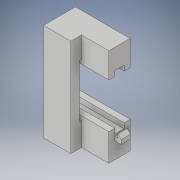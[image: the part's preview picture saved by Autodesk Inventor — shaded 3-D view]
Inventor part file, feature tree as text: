
AUTODESK INVENTOR PART (.ipt)
format: ipt  version: 2018 (Build 220112000, 112)  size: 337,920 bytes
history: native  units: in
note: dims shown in document units (in); Inventor stores cm internally (conversion verified against a paired STEP export)
features: extrude x19, sketch x18, projected_geometry x9, mirror x2, plane x1
ambient origin geometry x8: Origin, YZ Plane, XZ Plane, XY Plane, X Axis, Y Axis, Z Axis, Center Point
bodies: Solid1 (feature_tree)
feature tree (49):
  extrude  "Extrusion1"  Depth=9.0in
  extrude  "Extrusion2"  Depth=15.7in
  extrude  "Extrusion3"  Depth=0.5in
  extrude  "Extrusion4"  Depth=0.5in TaperAngle=0.0deg
  extrude  "Extrusion5"  Depth=1.05in
  extrude  "Extrusion6"  Depth=18.0in TaperAngle=0.0deg
  extrude  "Extrusion7"  Depth=3.25in
  extrude  "Extrusion11"  Depth=3.45in
  extrude  "Extrusion12"  Depth=3.25in
  plane  "Work Plane1"
  mirror  "Mirror1"
  extrude  "Extrusion14"  Depth=2.1in TaperAngle=0.0deg
  extrude  "Extrusion15"  Depth=0.75in TaperAngle=0.0deg
  extrude  "Extrusion16"  Depth=0.75in
  extrude  "Extrusion17"  Depth=0.75in
  mirror  "Mirror2"
  extrude  "Extrusion18"  Depth=4.95in
  extrude  "Extrusion19"  Depth=4.95in
  extrude  "Extrusion20"  TaperAngle=0.0deg  [1 undecoded]
  extrude  "Extrusion8"  Depth=1.5in TaperAngle=0.0deg
  extrude  "Extrusion9"  Depth=0.12in
  extrude  "Extrusion10"  Depth=0.14in
  sketch  "Sketch1"  dims[d0=16.7in d1=9.0in]
  sketch  "Sketch2"  dims[d2=6.5in d3=0.0in d4=15.7in]
  sketch  "Sketch4"  dims[d5=6.5in d6=0.5in]
  projected_geometry  "Projected Loop1"
  sketch  "Sketch5"  dims[d7=0.5in d8=5.85in d9=0.0in]
  projected_geometry  "Projected Loop2"
  sketch  "Sketch7"  dims[d10=3.775in d11=1.05in]
  projected_geometry  "Projected Loop4"
  sketch  "Sketch8"  dims[d12=2.475in d13=18.0in d14=0.0in]
  projected_geometry  "Projected Loop5"
  sketch  "Sketch9"  dims[d15=3.45in d16=3.25in]
  projected_geometry  "Projected Loop6"
  sketch  "Sketch10"  dims[d17=2.3in d18=3.45in]
  projected_geometry  "Projected Loop7"
  sketch  "Sketch11"  dims[d19=3.7in d20=3.25in]
  sketch  "Sketch12"  dims[d21=3.0in d22=0.0in d23=2.1in d24=0.0in]
  projected_geometry  "Projected Loop8"
  sketch  "Sketch13"  dims[d25=0.75in d26=0.0in d27=0.75in d28=0.0in]
  projected_geometry  "Projected Loop9"
  sketch  "Sketch15"  dims[d29=0.75in d30=0.75in]
  sketch  "Sketch17"  dims[d31=0.75in d32=0.75in]
  sketch  "Sketch18"  dims[d33=4.95in d34=4.95in]
  sketch  "Sketch19"  dims[d35=4.95in d36=4.95in]
  projected_geometry  "Projected Loop10"
  sketch  "Sketch21"  dims[d37=4.0in d38=0.0in d39=0.0in]
  sketch  "Sketch22"  dims[d40=1.5in d41=0.0in d42=1.5in d43=0.0in]
  sketch  "Sketch23"  dims[d44=0.22in d45=0.12in d46=0.14in d47=3.25in d48=0.0in d49=0.2in d50=0.0in d55=0.22in d56=0.075in d57=0.15in d58=0.0in d60=0.15in d61=0.04in d62=1.0in d63=0.0in d64=0.075in d65=0.081in d66=0.22in d67=0.0in d68=0.06in d69=0.0in d70=1.0in d71=0.0in d72=0.25in d73=0.0in d74=0.05in d75=0.1in d76=0.1in d77=1.0in d78=0.0in]
note: 1 required parameter value undecoded (feature->parameter linkage not recoverable at this tier; creation-order binding heuristic only, values carry confidence <= 0.55)
